# Revit family: DF_ЗажимПараллельный_Пруток_Стержень_8-10_16_EZETEK_
name_source: partatom
category: Соединительные детали воздуховодов
revit_build: Autodesk Revit 2017 (Build: 20170118_1100(x64)
units: mm (PartAtom-declared; Revit-internal decimal feet)

## family parameters
Всегда вертикально = Да
На основе рабочей плоскости = Нет
Общий = Нет
При загрузке вырезать с полостями = Нет
Размер круглого соединителя = Использовать радиус
Тип детали = Соединение

## types (3) — shared parameters
ADSK_Версия Revit = 2017
ADSK_Единица измерения = Неспецифицируемое
ADSK_Завод-изготовитель = Неспецифицируемое
ADSK_Код изделия = Неспецифицируемое
ADSK_Марка = Неспецифицируемое
ADSK_Масса_Текст = Неспецифицируемое
ADSK_Наименование = Неспецифицируемое
ADSK_Обозначение = Неспецифицируемое
URL = https://ezetek.ru
Группа модели = Зажимы
Изготовитель = Ezetek
Описание = Зажим выполнен из оцинкованной стали и используется для соединения в параллельном направлении прутка молниезащитной сетки диаметром 8-10 мм со стрежнем либо молниеприемником диаметром 16 мм.
Угол = 90.00°
zero-valued in all types: ADSK_Количество, ADSK_Масса

## per-type parameters (varying)
| type | ADSK_Материал | Тип |
| ЗажимПараллельный_Стержень-Стержень_Латунь_90553 | BIMLIB_Латунь_EZETEK | PF_ЗажимПараллельный_Пруток_Стержень_8-10_16_EZETEK : ЗажимПараллельный_Пруток_Стержень_Латунь_90553 |
| ЗажимПараллельный_Стержень-Стержень_СтальОцинкованная_90550 | BIMLIB_Сталь_Оцинкованная_EZETEK | PF_ЗажимПараллельный_Пруток_Стержень_8-10_16_EZETEK : ЗажимПараллельный_Пруток_Стержень_СтальОцинкованная_90550 |
| ЗажимПараллельный_Стержень-Стержень_Медь_90552 | BIMLIB_Латунь_EZETEK | PF_ЗажимПараллельный_Пруток_Стержень_8-10_16_EZETEK : ЗажимПараллельный_Пруток_Стержень_Медь_90552 |
